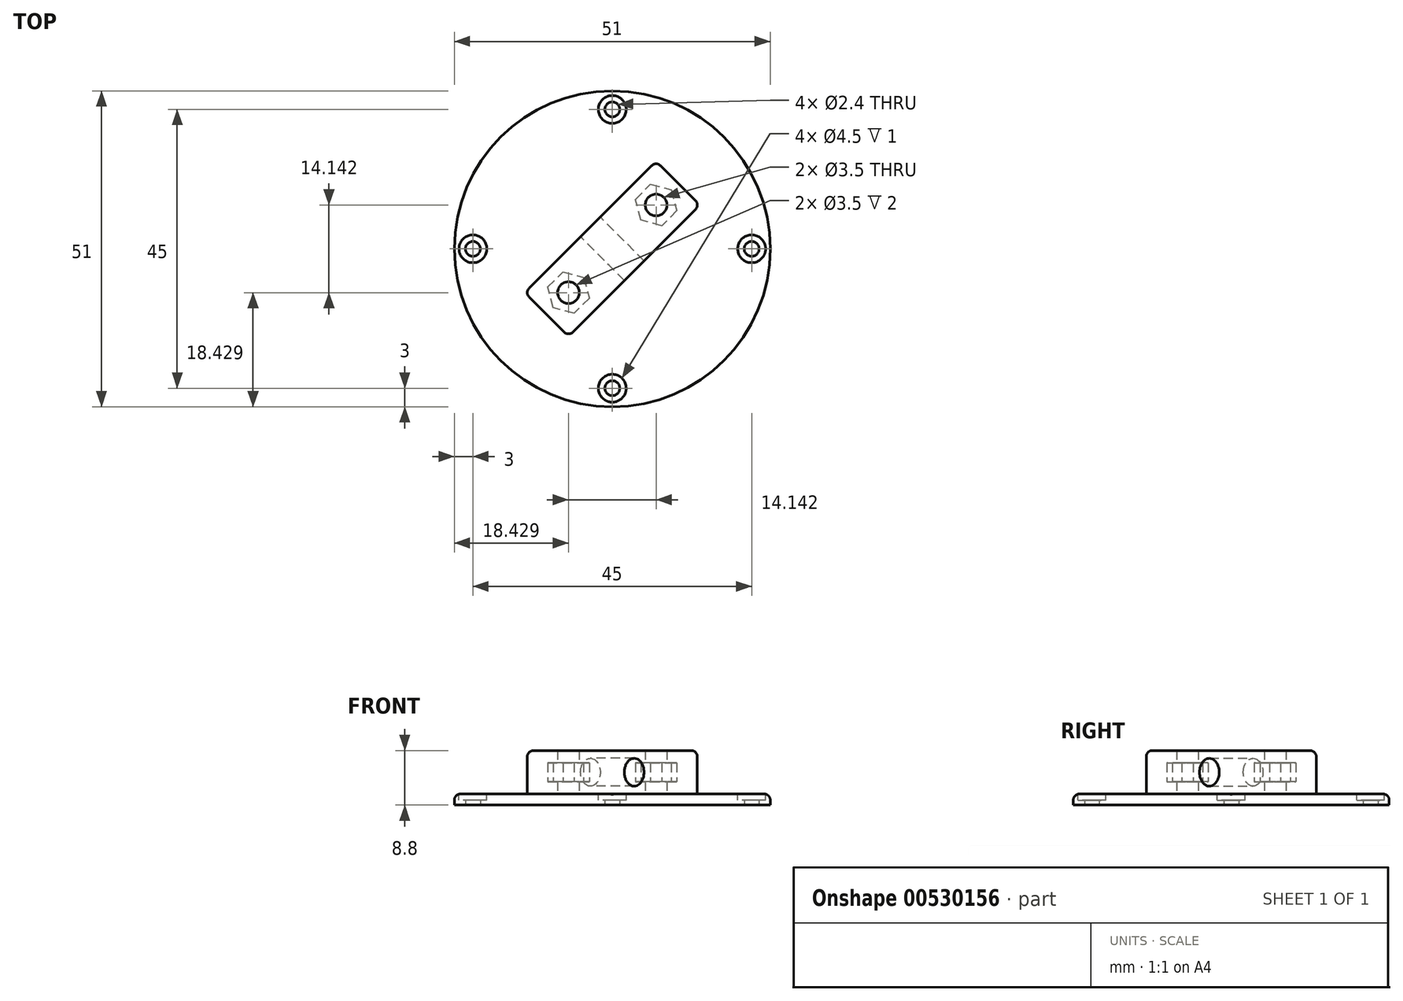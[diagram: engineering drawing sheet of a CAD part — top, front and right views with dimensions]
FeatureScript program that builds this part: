
annotation { "Feature Type Name" : "Feature", "Feature Type Description" : "" }
export const myFeature = defineFeature(function(context is Context, id is Id, definition is map)
    precondition{}
    {
        {
            var Q0;
            Q0=qCreatedBy(makeId("Top.planeOp"),FACE);
            var sketch = newSketch(context, id + "F0", { "sketchPlane" : qUnion([Q0])});
            skCircle(sketch, "E0", {"center": v(0, 0) * mm, "radius": 25.5 * mm});
            skCircle(sketch, "E1", {"center": v(0, 0) * mm, "radius": 22.5 * mm, "construction": true});
            skCircle(sketch, "E2", {"center": v(0, 22.5) * mm, "radius": 1.2 * mm});
            skCircle(sketch, "E3", {"center": v(-22.5, 0) * mm, "radius": 1.2 * mm});
            skCircle(sketch, "E4", {"center": v(0, -22.5) * mm, "radius": 1.2 * mm});
            skCircle(sketch, "E5", {"center": v(22.5, 0) * mm, "radius": 1.2 * mm});
            skSolve(sketch);
        }
        {
            var Q0;
            Q0=makeQuery(id+"F0.imprint","IMPRINT",FACE,{"disambiguationData":[TD([[makeQuery(id+"F0.imprint","IMPRINT",EDGE,{"derivedFrom":sQuery(id+"F0.wireOp",EDGE,"E0")}),1.0]])]});
            extrude(context, id + "F1", {"entities" : qUnion([Q0]), "depth" : 1.8 * mm, "offsetDistance" : 25 * mm});
        }
        {
            var Q0;
            Q0=makeQuery(id+"F1.opExtrude","CAP_FACE",FACE,{"disambiguationData":[OSD([sQuery(id+"F0.wireOp",EDGE,"E0"),sQuery(id+"F0.wireOp",EDGE,"E2"),sQuery(id+"F0.wireOp",EDGE,"E3"),sQuery(id+"F0.wireOp",EDGE,"E4"),sQuery(id+"F0.wireOp",EDGE,"E5")])],"isStart":false});
            var sketch = newSketch(context, id + "F2", { "sketchPlane" : qUnion([Q0])});
            skCircle(sketch, "E6", {"center": v(0, -22.5) * mm, "radius": 2.25 * mm});
            skCircle(sketch, "E7", {"center": v(-22.5, 0) * mm, "radius": 2.25 * mm});
            skCircle(sketch, "E8", {"center": v(0, 22.5) * mm, "radius": 2.25 * mm});
            skCircle(sketch, "E9", {"center": v(22.5, 0) * mm, "radius": 2.25 * mm});
            skSolve(sketch);
        }
        {
            var Q0;
            Q0 = qSketchRegion(id + "F2", true);
            extrude(context, id + "F3", {"entities" : qUnion([Q0]), "operationType" : NewBodyOperationType.REMOVE, "oppositeDirection" : true, "depth" : 1 * mm, "offsetDistance" : 25 * mm});
        }
        {
            var Q0;
            Q0=makeQuery(id+"F1.opExtrude","CAP_FACE",FACE,{"disambiguationData":[OSD([sQuery(id+"F0.wireOp",EDGE,"E0"),sQuery(id+"F0.wireOp",EDGE,"E2"),sQuery(id+"F0.wireOp",EDGE,"E3"),sQuery(id+"F0.wireOp",EDGE,"E4"),sQuery(id+"F0.wireOp",EDGE,"E5")])],"isStart":false});
            var sketch = newSketch(context, id + "F4", { "sketchPlane" : qUnion([Q0])});
            skLineSegment(sketch, "E10.bottom", {"start": v(-14.14, -7.07) * mm, "end": v(7.07, 14.14) * mm});
            skLineSegment(sketch, "E10.top", {"start": v(-7.07, -14.14) * mm, "end": v(14.14, 7.07) * mm});
            skLineSegment(sketch, "E10.left", {"start": v(-14.14, -7.07) * mm, "end": v(-7.07, -14.14) * mm});
            skLineSegment(sketch, "E10.right", {"start": v(7.07, 14.14) * mm, "end": v(14.14, 7.07) * mm});
            skPoint(sketch, "E10.middle", {"position": v(0, 0) * mm});
            skLineSegment(sketch, "E11", {"start": v(-7.07, -7.07) * mm, "end": v(0, 0) * mm, "construction": true});
            skLineSegment(sketch, "E12", {"start": v(7.07, 7.07) * mm, "end": v(0, 0) * mm, "construction": true});
            skCircle(sketch, "E13.cCircle", {"center": v(-7.07, -7.07) * mm, "radius": 3 * mm, "construction": true});
            skLineSegment(sketch, "E13.0", {"start": v(-9.52, -9.52) * mm, "end": v(-10.42, -6.17) * mm});
            skLineSegment(sketch, "E13.1", {"start": v(-10.42, -6.17) * mm, "end": v(-7.97, -3.73) * mm});
            skLineSegment(sketch, "E13.2", {"start": v(-7.97, -3.73) * mm, "end": v(-4.62, -4.62) * mm});
            skLineSegment(sketch, "E13.3", {"start": v(-4.62, -4.62) * mm, "end": v(-3.73, -7.97) * mm});
            skLineSegment(sketch, "E13.4", {"start": v(-3.73, -7.97) * mm, "end": v(-6.17, -10.42) * mm});
            skLineSegment(sketch, "E13.5", {"start": v(-6.17, -10.42) * mm, "end": v(-9.52, -9.52) * mm});
            skPoint(sketch, "E13.0.midPoint", {"position": v(-9.97, -7.85) * mm});
            skCircle(sketch, "E14.cCircle", {"center": v(7.07, 7.07) * mm, "radius": 3 * mm, "construction": true});
            skLineSegment(sketch, "E14.0", {"start": v(6.17, 10.42) * mm, "end": v(9.52, 9.52) * mm});
            skLineSegment(sketch, "E14.1", {"start": v(9.52, 9.52) * mm, "end": v(10.42, 6.17) * mm});
            skLineSegment(sketch, "E14.2", {"start": v(10.42, 6.17) * mm, "end": v(7.97, 3.73) * mm});
            skLineSegment(sketch, "E14.3", {"start": v(7.97, 3.73) * mm, "end": v(4.62, 4.62) * mm});
            skLineSegment(sketch, "E14.4", {"start": v(4.62, 4.62) * mm, "end": v(3.73, 7.97) * mm});
            skLineSegment(sketch, "E14.5", {"start": v(3.73, 7.97) * mm, "end": v(6.17, 10.42) * mm});
            skPoint(sketch, "E14.0.midPoint", {"position": v(7.85, 9.97) * mm});
            skCircle(sketch, "E15", {"center": v(-7.07, -7.07) * mm, "radius": 1.75 * mm});
            skCircle(sketch, "E16", {"center": v(7.07, 7.07) * mm, "radius": 1.75 * mm});
            skSolve(sketch);
        }
        {
            var Q0;
            Q0=makeQuery(id+"F4.imprint","IMPRINT",FACE,{"disambiguationData":[TD([[makeQuery(id+"F4.imprint","IMPRINT",EDGE,{"derivedFrom":sQuery(id+"F4.wireOp",EDGE,"E10.bottom")}),-1.0]])]});
            var Q1;
            Q1=makeQuery(id+"F4.imprint","IMPRINT",FACE,{"disambiguationData":[TD([[makeQuery(id+"F4.imprint","IMPRINT",EDGE,{"derivedFrom":sQuery(id+"F4.wireOp",EDGE,"E13.0")}),-1.0]])]});
            var Q2;
            Q2=makeQuery(id+"F4.imprint","IMPRINT",FACE,{"disambiguationData":[TD([[makeQuery(id+"F4.imprint","IMPRINT",EDGE,{"derivedFrom":sQuery(id+"F4.wireOp",EDGE,"E14.0")}),-1.0]])]});
            extrude(context, id + "F5", {"entities" : qUnion([Q0, Q1, Q2]), "operationType" : NewBodyOperationType.ADD, "depth" : 7 * mm, "offsetDistance" : 25 * mm});
        }
        {
            var Q0;
            Q0=makeQuery(id+"F4.imprint","IMPRINT",FACE,{"disambiguationData":[TD([[makeQuery(id+"F4.imprint","IMPRINT",EDGE,{"derivedFrom":sQuery(id+"F4.wireOp",EDGE,"E13.0")}),-1.0]])]});
            var Q1;
            Q1=makeQuery(id+"F4.imprint","IMPRINT",FACE,{"disambiguationData":[TD([[makeQuery(id+"F4.imprint","IMPRINT",EDGE,{"derivedFrom":sQuery(id+"F4.wireOp",EDGE,"E14.0")}),-1.0]])]});
            extrude(context, id + "F6", {"entities" : qUnion([Q0, Q1]), "operationType" : NewBodyOperationType.REMOVE, "depth" : 5 * mm, "offsetDistance" : 25 * mm, "hasSecondDirection" : true, "secondDirectionOppositeDirection" : false, "secondDirectionDepth" : 2 * mm});
        }
        {
            var Q0;
            Q0=makeQuery(id+"F5.opExtrude","SWEPT_FACE",FACE,{"disambiguationData":[OSD([sQuery(id+"F4.wireOp",EDGE,"E10.bottom")])]});
            var sketch = newSketch(context, id + "F7", { "sketchPlane" : qUnion([Q0])});
            skLineSegment(sketch, "E17", {"start": v(-15, 8.8) * mm, "end": v(15, 1.8) * mm, "construction": true});
            skCircle(sketch, "E18", {"center": v(0, 5.3) * mm, "radius": 2.25 * mm});
            skSolve(sketch);
        }
        {
            var Q0;
            Q0=makeQuery(id+"F7.imprint","IMPRINT",FACE,{"disambiguationData":[TD([[makeQuery(id+"F7.imprint","IMPRINT",EDGE,{"derivedFrom":sQuery(id+"F7.wireOp",EDGE,"E18")}),1.0]])]});
            extrude(context, id + "F8", {"entities" : qUnion([Q0]), "operationType" : NewBodyOperationType.REMOVE, "endBound" : BoundingType.THROUGH_ALL, "oppositeDirection" : true, "depth" : 25 * mm, "offsetDistance" : 25 * mm});
        }
        {
            var Q0;
            Q0=makeQuery(id+"F1.opExtrude","CAP_EDGE",EDGE,{"disambiguationData":[OSD([sQuery(id+"F0.wireOp",EDGE,"E0")])],"isStart":false});
            var Q1;
            Q1=makeQuery(id+"F5.opExtrude","SWEPT_EDGE",EDGE,{"disambiguationData":[OSD([sQuery(id+"F4.wireOp",EDGE,"E10.bottom"),sQuery(id+"F4.wireOp",EDGE,"E10.left")])]});
            var Q2;
            Q2=makeQuery(id+"F5.opExtrude","SWEPT_EDGE",EDGE,{"disambiguationData":[OSD([sQuery(id+"F4.wireOp",EDGE,"E10.top"),sQuery(id+"F4.wireOp",EDGE,"E10.left")])]});
            var Q3;
            Q3=makeQuery(id+"F5.opExtrude","CAP_EDGE",EDGE,{"disambiguationData":[OSD([sQuery(id+"F4.wireOp",EDGE,"E10.left")])],"isStart":false});
            var Q4;
            Q4=makeQuery(id+"F5.opExtrude","CAP_EDGE",EDGE,{"disambiguationData":[OSD([sQuery(id+"F4.wireOp",EDGE,"E10.bottom")])],"isStart":false});
            var Q5;
            Q5=makeQuery(id+"F5.opExtrude","CAP_EDGE",EDGE,{"disambiguationData":[OSD([sQuery(id+"F4.wireOp",EDGE,"E10.top")])],"isStart":false});
            var Q6;
            Q6=makeQuery(id+"F5.opExtrude","CAP_EDGE",EDGE,{"disambiguationData":[OSD([sQuery(id+"F4.wireOp",EDGE,"E10.right")])],"isStart":false});
            var Q7;
            Q7=makeQuery(id+"F5.opExtrude","SWEPT_EDGE",EDGE,{"disambiguationData":[OSD([sQuery(id+"F4.wireOp",EDGE,"E10.top"),sQuery(id+"F4.wireOp",EDGE,"E10.right")])]});
            var Q8;
            Q8=makeQuery(id+"F5.opExtrude","SWEPT_EDGE",EDGE,{"disambiguationData":[OSD([sQuery(id+"F4.wireOp",EDGE,"E10.bottom"),sQuery(id+"F4.wireOp",EDGE,"E10.right")])]});
            fillet(context, id + "F9", {"entities" : qUnion([Q0, Q1, Q2, Q3, Q4, Q5, Q6, Q7, Q8]), "tangentPropagation" : true, "radius" : 1 * mm, "defaultsChanged" : false, "vertexSettings" : [], "allowEdgeOverflow" : false});
        }
    });
